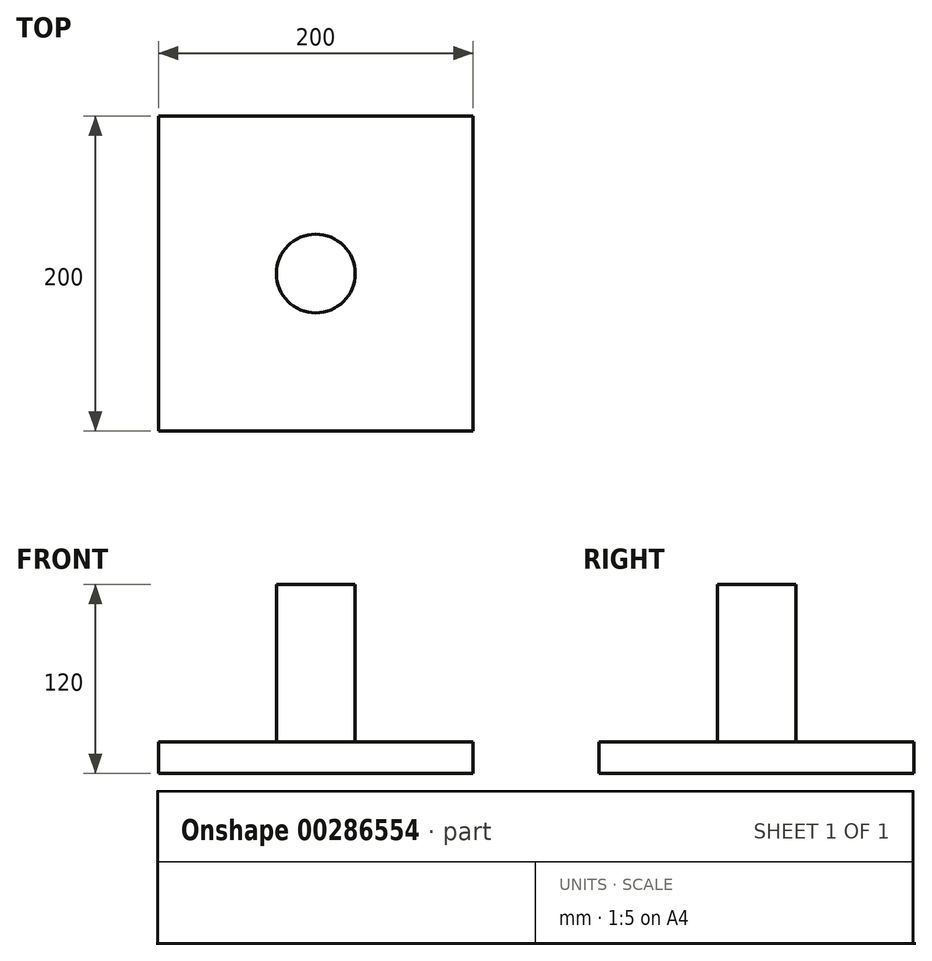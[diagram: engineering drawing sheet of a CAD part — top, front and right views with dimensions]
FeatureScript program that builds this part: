
annotation { "Feature Type Name" : "Feature", "Feature Type Description" : "" }
export const myFeature = defineFeature(function(context is Context, id is Id, definition is map)
    precondition{}
    {
        {
            var Q0;
            Q0=qCreatedBy(makeId("Top.planeOp"),FACE);
            var sketch = newSketch(context, id + "F0", { "sketchPlane" : qUnion([Q0])});
            skLineSegment(sketch, "E0.bottom", {"start": v(0, 0) * mm, "end": v(200, 0) * mm});
            skLineSegment(sketch, "E0.top", {"start": v(0, -200) * mm, "end": v(200, -200) * mm});
            skLineSegment(sketch, "E0.left", {"start": v(0, 0) * mm, "end": v(0, -200) * mm});
            skLineSegment(sketch, "E0.right", {"start": v(200, 0) * mm, "end": v(200, -200) * mm});
            skSolve(sketch);
        }
        {
            var Q0;
            Q0=qSketchRegion(id+"F0",true);
            extrude(context, id + "F1", {"entities" : qUnion([Q0]), "depth" : 20 * mm});
        }
        {
            var Q0;
            Q0=makeQuery(id+"F1.opExtrude","CAP_FACE",FACE,{"disambiguationData":[OSD([sQuery(id+"F0.wireOp",EDGE,"E0.bottom"),sQuery(id+"F0.wireOp",EDGE,"E0.top"),sQuery(id+"F0.wireOp",EDGE,"E0.left"),sQuery(id+"F0.wireOp",EDGE,"E0.right")])],"isStart":false});
            var sketch = newSketch(context, id + "F2", { "sketchPlane" : qUnion([Q0])});
            skCircle(sketch, "E1", {"center": v(100, -100) * mm, "radius": 25 * mm});
            skSolve(sketch);
        }
        {
            var Q0;
            Q0=makeQuery(id+"F2.imprint","IMPRINT",FACE,{"disambiguationData":[TD([[makeQuery(id+"F2.imprint","IMPRINT",EDGE,{"derivedFrom":sQuery(id+"F2.wireOp",EDGE,"E1")}),1.0]])]});
            extrude(context, id + "F3", {"entities" : qUnion([Q0]), "operationType" : NewBodyOperationType.ADD, "depth" : 100 * mm});
        }
    });
